# Revit family: QF_BPRO_UNI 59-29_574911
name_source: partatom
category: Sonderausstattung
revit_build: Autodesk Revit 2018 (Build: 20190510_1515(x64)
units: mm (PartAtom-declared; Revit-internal decimal feet)

## family parameters
Arbeitsebenenbasiert = Nein
Beim Laden mit Abzugskörper schneiden = Nein
Bemaßung runder Anschluss = Durchmesser verwenden
Gemeinsam genutzt = Nein
Immer vertikal = Ja
Raumberechnungspunkt = Ja
Teiletyp = Normal

## types (1)
- UNI 59-29
    Abdeckhaube Höhe = 127 mm
    Abdeckhaube Länge = 642 mm  [stored 2.1063 ft]
    Abdeckhaube Tiefe = 342 mm  [stored 1.12205 ft]
    Abstand Plattform Hinten = 42 mm
    Artikel Nummer = 574911
    Beschreibung = inkl. Abdeckhaube aus EPP;
    Beschreibung durch Hersteller analog Leistungsverzeichniskurztext = Abmessungen

Länge:					  740 mm
Breite:					  520 mm
Höhe:					  944mm
Höhe (mit Option Abdeckhaube)		1027 mm
Arbeitshöhe:					  900 mm


Ausführung

Aufbau
Der Universalspender besteht komplett aus CNS 18/10. Die Oberfläche ist mikroliert.
Der Korpus ist einwandig und kompakt in geschlossener Ausführung aufgebaut. Der Universalspender hat eine durchgehende pulverbeschichtete Innenverkleidung, um Streifspuren am Geschirr zu vermeiden.
Durch die Rastereinteilung der Plattform können mithilfe der 6 variabel einteilbaren Kunststoff- Führungsschienen die unterschiedlichsten Geschirrarten gestapelt werden.
Die Stapelplattform ist leichtgängig und durch Führungen mit kugelgelagerten Rollen gegen Kippen und Verkanten gesichert.
Durch Ein- bzw. Aushängen der Zugfedern kann die Federspannung entsprechend dem Stapelgut reguliert werden, um eine gleichbleibende Ausgabehöhe zu gewährleisten.
Bedienseitig ist ein CNS-Sicherheits-Schiebegriff mit seitlichen Stoßschutzelementen aus Kunststoff (Polyamid) angebracht.
Fahrbar ist der Spender mittels rostfreien Kunststoffrollen (4 Lenkrollen, 2 davon mit Feststeller mit 125 mm ø). Massive Stoßecken aus Kunststoff (Polyamid) an allen vier Ecken schützen vor Beschädigung.


Zubehör/ Optionen

•	Abdeckhaube (642 x 342 mm), Polycarbonat
Stapelhöhe mit Abdeckhaube		680 mm
Stapelhöhe ohne Abdeckhaube:	540 mm
•	Weitere Zubehöre und Rollenausführungen siehe Gesamt-Preisliste


Technische Daten

Werkstoff:		CNS 18/10
Gewicht:		48,5 kg 
Lichtes Maß:		590 x 290 mm
Kapazität:		abhängig von der Geschirrart



Besonderheit

•	Veränderung der Federspannung möglich
•	variable Einstellungen durch 6 Führungsstäbe
•	gemäß DIN 18665, Teil 6 


Fabrikat

Hersteller:			B.PRO
Modell:				UNI 59/ 29		
Best.Nr.			574 911
    Beschreibung durch Hersteller analog Leistungsverzeichnislangtext = Abmessungen

Länge:					  740 mm
Breite:					  520 mm
Höhe:					  944mm
Höhe (mit Option Abdeckhaube)		1027 mm
Arbeitshöhe:					  900 mm


Ausführung

Aufbau
Der Universalspender besteht komplett aus CNS 18/10. Die Oberfläche ist mikroliert.
Der Korpus ist einwandig und kompakt in geschlossener Ausführung aufgebaut. Der Universalspender hat eine durchgehende pulverbeschichtete Innenverkleidung, um Streifspuren am Geschirr zu vermeiden.
Durch die Rastereinteilung der Plattform können mithilfe der 6 variabel einteilbaren Kunststoff- Führungsschienen die unterschiedlichsten Geschirrarten gestapelt werden.
Die Stapelplattform ist leichtgängig und durch Führungen mit kugelgelagerten Rollen gegen Kippen und Verkanten gesichert.
Durch Ein- bzw. Aushängen der Zugfedern kann die Federspannung entsprechend dem Stapelgut reguliert werden, um eine gleichbleibende Ausgabehöhe zu gewährleisten.
Bedienseitig ist ein CNS-Sicherheits-Schiebegriff mit seitlichen Stoßschutzelementen aus Kunststoff (Polyamid) angebracht.
Fahrbar ist der Spender mittels rostfreien Kunststoffrollen (4 Lenkrollen, 2 davon mit Feststeller mit 125 mm ø). Massive Stoßecken aus Kunststoff (Polyamid) an allen vier Ecken schützen vor Beschädigung.


Zubehör/ Optionen

•	Abdeckhaube (642 x 342 mm), Polycarbonat
Stapelhöhe mit Abdeckhaube		680 mm
Stapelhöhe ohne Abdeckhaube:	540 mm
•	Weitere Zubehöre und Rollenausführungen siehe Gesamt-Preisliste


Technische Daten

Werkstoff:		CNS 18/10
Gewicht:		48,5 kg 
Lichtes Maß:		590 x 290 mm
Kapazität:		abhängig von der Geschirrart



Besonderheit

•	Veränderung der Federspannung möglich
•	variable Einstellungen durch 6 Führungsstäbe
•	gemäß DIN 18665, Teil 6 


Fabrikat

Hersteller:			B.PRO
Modell:				UNI 59/ 29		
Best.Nr.			574 911
    Gerätegewicht Netto = 48.50 kg
    Großküchengerätezuordnung = Ja
    Hersteller = B.PRO GmbH
    Höhe Korpus = 900 mm  [stored 2.95276 ft]
    Internetadresse Gerätehersteller = https://www.bpro-solutions.com
    Internetadresse für Ersatzteilliste = https://www.bpro-solutions.com
    Kosten = 1918.4 $
    Länge Gerätebreite = 775 mm
    Länge Korpus = 670 mm  [stored 2.19816 ft]
    Material = QF_Metal-Stainless-Steel_general
    Material_Stoßschutz = QF_Rubber-Black-Matt
    Modell = UNI 59-29
    Plattform Länge = 590 mm  [stored 1.9357 ft]
    Plattform Tiefe = 290 mm  [stored 0.951444 ft]
    Schacht Tiefe = 600 mm
    Sockelhöhe = 161 mm  [stored 0.528215 ft]
    Tiefe = 520 mm  [stored 1.70604 ft]
    Tiefe Korpus = 450 mm  [stored 1.47638 ft]
    Typenkommentare = Universalspender, unbeheizt
    URL = https://www.bpro-solutions.com
    Warnhinweise = Ausführliche Gefahrenhinweise entnehmen Sie der Betriebsanleitung.
    Zubehör = Nein

note: [stored X ft] marks values corroborated as IEEE doubles in the binary element streams (Revit-internal decimal feet)
